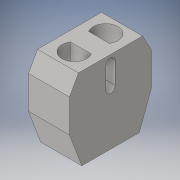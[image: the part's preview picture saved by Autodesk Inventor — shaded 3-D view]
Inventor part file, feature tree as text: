
AUTODESK INVENTOR PART (.ipt)
format: ipt  version: 2016 (Build 200138000, 138)  size: 188,416 bytes
history: native  units: in
note: dims shown in document units (in); Inventor stores cm internally (conversion verified against a paired STEP export)
features: sketch x12, extrude x9, revolve x2, plane x1
ambient origin geometry x8: Origin, YZ Plane, XZ Plane, XY Plane, X Axis, Y Axis, Z Axis, Center Point
bodies: Solid1 (feature_tree)
feature tree (24):
  extrude  "Extrusion1"  Depth=1.0in
  sketch  "Sketch2"  dims[d2=0.5in d3=0.0in d4=0.04in]
  plane  "Work Plane1"
  revolve  "Revolution1"  [1 undecoded]
  revolve  "Revolution2"  Angle=90.0deg
  extrude  "Extrusion2"  TaperAngle=90.0deg  [1 undecoded]
  extrude  "Extrusion3"  Depth=0.15in
  extrude  "Extrusion4"  Depth=0.15in
  extrude  "Extrusion5"  Depth=0.5in TaperAngle=0.0deg
  extrude  "Extrusion6"  Depth=0.11in
  extrude  "Extrusion7"  Depth=0.11in
  extrude  "Extrusion8"  Depth=0.5in TaperAngle=0.0deg
  extrude  "Extrusion9"  Depth=0.5in TaperAngle=0.0deg
  sketch  "Sketch1"  dims[d0=1.0in d1=1.0in]
  sketch  "Sketch3"  dims[d5=0.04in d6=90.0deg]
  sketch  "Sketch4"  dims[d7=0.3in d8=90.0deg]
  sketch  "Sketch5"  dims[d9=0.15in d10=0.4in]
  sketch  "Sketch6"  dims[d11=0.5in d12=0.0in d13=0.15in]
  sketch  "Sketch7"  dims[d14=0.4in d15=0.5in d16=0.0in]
  sketch  "Sketch8"  dims[d17=0.11in d18=0.2in]
  sketch  "Sketch9"  dims[d19=0.5in d20=0.0in d21=0.11in]
  sketch  "Sketch10"  dims[d22=0.2in d23=0.5in d24=0.0in]
  sketch  "Sketch11"  dims[d25=0.5in d26=0.0in d28=0.5in d29=0.0in]
  sketch  "Sketch12"  dims[d30=0.5in d31=0.0in d32=0.112in d33=1.0in d34=0.0in]
note: 2 required parameter values undecoded (feature->parameter linkage not recoverable at this tier; creation-order binding heuristic only, values carry confidence <= 0.55)